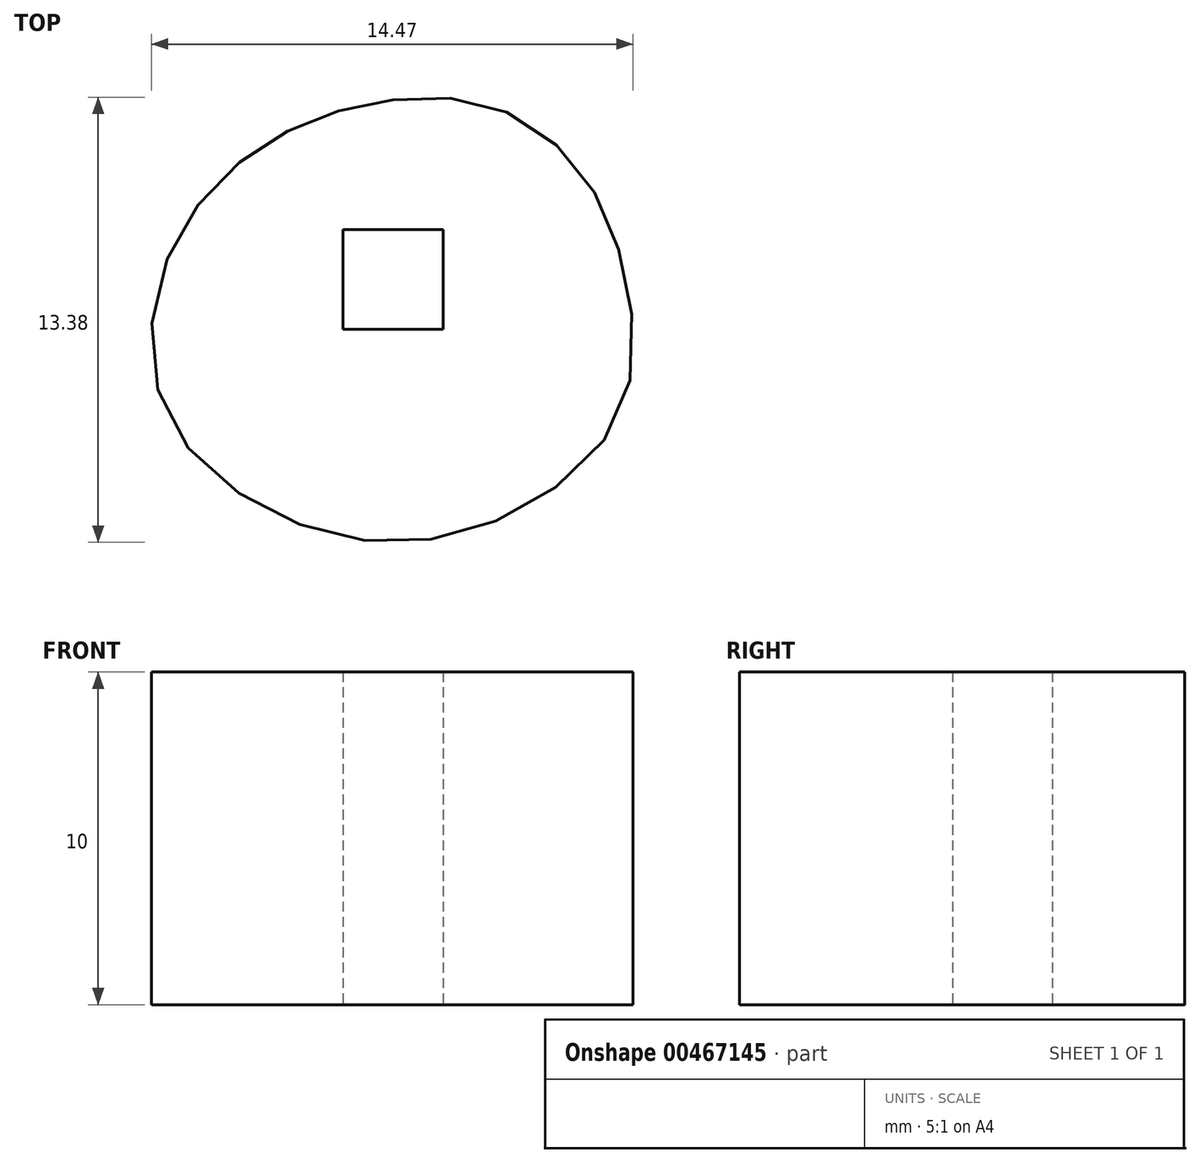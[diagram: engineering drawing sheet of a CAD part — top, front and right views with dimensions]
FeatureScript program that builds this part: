
annotation { "Feature Type Name" : "Feature", "Feature Type Description" : "" }
export const myFeature = defineFeature(function(context is Context, id is Id, definition is map)
    precondition{}
    {
        {
            var Q0;
            Q0=qCreatedBy(makeId("Top.planeOp"),FACE);
            var sketch = newSketch(context, id + "F0", { "sketchPlane" : qUnion([Q0])});
            skLineSegment(sketch, "E0", {"start": v(0, 0) * mm, "end": v(0, 5.4) * mm, "construction": true});
            skLineSegment(sketch, "E1", {"start": v(0, 0) * mm, "end": v(3, 5.2) * mm, "construction": true});
            skLineSegment(sketch, "E2", {"start": v(0, 0) * mm, "end": v(5.63, 3.25) * mm, "construction": true});
            skLineSegment(sketch, "E3", {"start": v(0, 0) * mm, "end": v(7, 0) * mm, "construction": true});
            skLineSegment(sketch, "E4", {"start": v(0, 0) * mm, "end": v(0, -7.9) * mm, "construction": true});
            skLineSegment(sketch, "E5", {"start": v(0, 0) * mm, "end": v(3.95, -6.84) * mm, "construction": true});
            skLineSegment(sketch, "E6", {"start": v(0, 0) * mm, "end": v(6.84, -3.95) * mm, "construction": true});
            skLineSegment(sketch, "E7", {"start": v(0, 0) * mm, "end": v(-3.95, -6.84) * mm, "construction": true});
            skLineSegment(sketch, "E8", {"start": v(0, 0) * mm, "end": v(-6.84, -3.95) * mm, "construction": true});
            skLineSegment(sketch, "E9", {"start": v(0, 0) * mm, "end": v(-7, 0) * mm, "construction": true});
            skLineSegment(sketch, "E10", {"start": v(0, 0) * mm, "end": v(-5.2, 3) * mm, "construction": true});
            skLineSegment(sketch, "E11", {"start": v(0, 0) * mm, "end": v(-2.7, 4.68) * mm, "construction": true});
            skFitSpline(sketch, "E12", {"points": [v(0, 5.4) * mm, v(3, 5.2) * mm, v(5.63, 3.25) * mm, v(7, 0) * mm, v(6.84, -3.95) * mm, v(3.95, -6.84) * mm, v(0, -7.9) * mm, v(-3.95, -6.84) * mm, v(-6.84, -3.95) * mm, v(-7, 0) * mm, v(-5.2, 3) * mm, v(-2.7, 4.68) * mm, v(0, 5.4) * mm]});
            skLineSegment(sketch, "E13.bottom", {"start": v(-1.5, -1.5) * mm, "end": v(1.5, -1.5) * mm});
            skLineSegment(sketch, "E13.top", {"start": v(-1.5, 1.5) * mm, "end": v(1.5, 1.5) * mm});
            skLineSegment(sketch, "E13.left", {"start": v(-1.5, -1.5) * mm, "end": v(-1.5, 1.5) * mm});
            skLineSegment(sketch, "E13.right", {"start": v(1.5, -1.5) * mm, "end": v(1.5, 1.5) * mm});
            skPoint(sketch, "E13.middle", {"position": v(0, 0) * mm});
            skSolve(sketch);
        }
        {
            var Q0;
            Q0=makeQuery(id+"F0.imprint","IMPRINT",FACE,{"disambiguationData":[TD([[makeQuery(id+"F0.imprint","IMPRINT",EDGE,{"derivedFrom":sQuery(id+"F0.wireOp",EDGE,"E12")}),-1.0]])]});
            extrude(context, id + "F1", {"entities" : qUnion([Q0]), "endBound" : BoundingType.SYMMETRIC, "depth" : 10 * mm, "offsetDistance" : 25 * mm});
        }
    });
